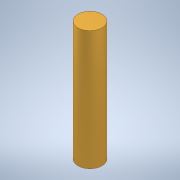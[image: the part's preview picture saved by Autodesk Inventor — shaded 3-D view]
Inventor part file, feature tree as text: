
AUTODESK INVENTOR PART (.ipt)
format: ipt  version: 2022.4 (Build 264492010, 492A)  size: 110,080 bytes
history: native  units: mm
features: sketch x2, other x1, extrude x1
ambient origin geometry x8: Origin, YZ Plane, XZ Plane, XY Plane, X Axis, Y Axis, Z Axis, Center Point
bodies: Solid2 (feature_tree), Solid1 (feature_tree)
feature tree (4):
  other  "Repaired Geometry1"
  extrude  "Extrusion1"  TaperAngle=0.0deg  [1 undecoded]
  sketch  "Sketch1"  dims[d0=10.0mm d1=0.0mm d2=0.0mm]
  sketch  "Sketch2"
note: 1 required parameter value undecoded (feature->parameter linkage not recoverable at this tier; creation-order binding heuristic only, values carry confidence <= 0.55)
